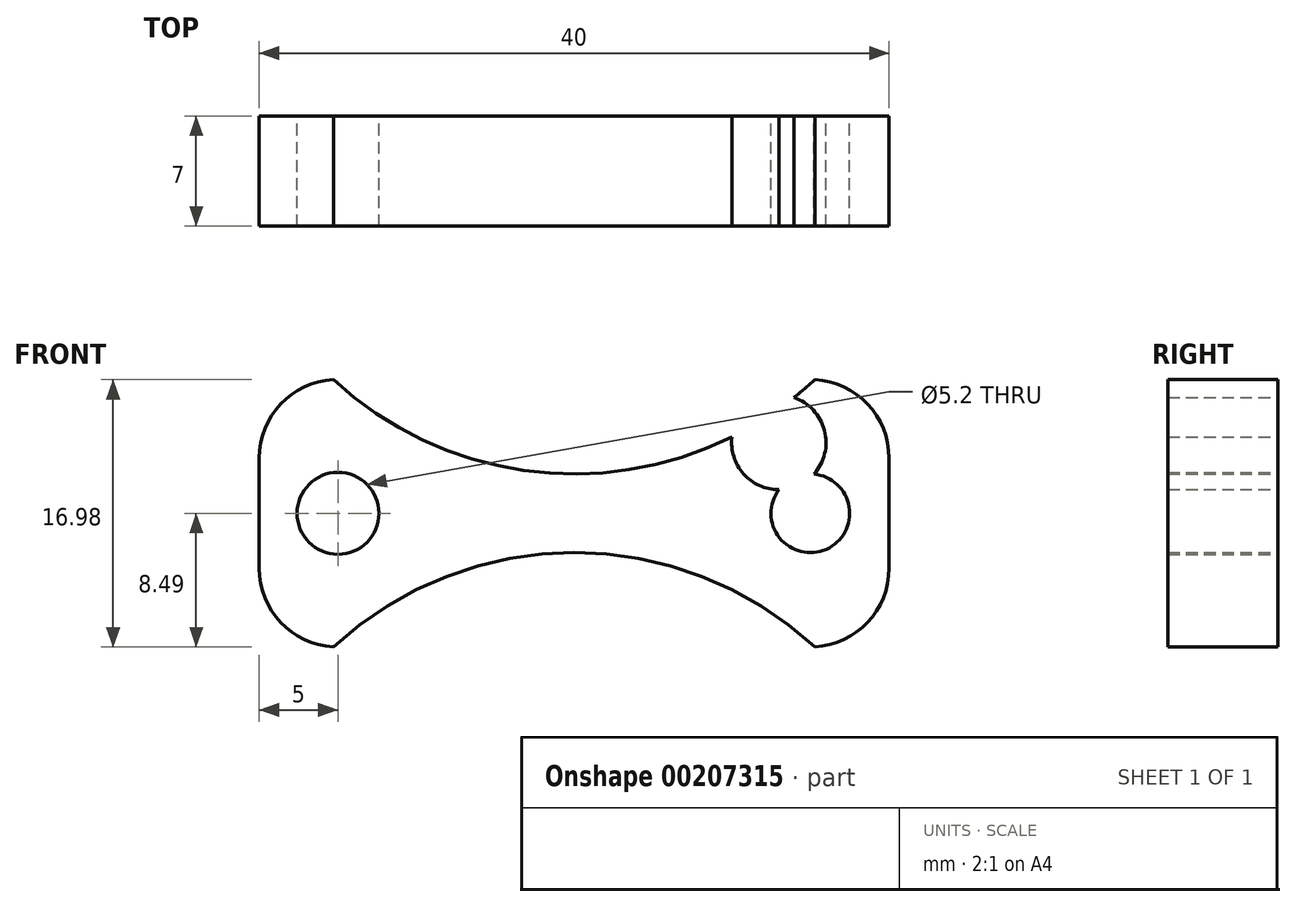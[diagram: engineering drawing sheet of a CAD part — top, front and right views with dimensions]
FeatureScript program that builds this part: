
annotation { "Feature Type Name" : "Feature", "Feature Type Description" : "" }
export const myFeature = defineFeature(function(context is Context, id is Id, definition is map)
    precondition{}
    {
        {
            var Q0;
            Q0=qCreatedBy(makeId("Front.planeOp"),FACE);
            var sketch = newSketch(context, id + "F0", { "sketchPlane" : qUnion([Q0])});
            skLineSegment(sketch, "E0.bottom", {"start": v(15, -8.5) * mm, "end": v(-15, -8.5) * mm});
            skLineSegment(sketch, "E0.top", {"start": v(15, 8.5) * mm, "end": v(-15, 8.5) * mm});
            skLineSegment(sketch, "E0.left", {"start": v(20, -3.5) * mm, "end": v(20, 3.5) * mm});
            skLineSegment(sketch, "E0.right", {"start": v(-20, -3.5) * mm, "end": v(-20, 3.5) * mm});
            skPoint(sketch, "E0.middle", {"position": v(0, 0) * mm});
            skPoint(sketch, "E1.visualSharp", {"position": v(-20, 8.5) * mm});
            skArc(sketch, "E1.filletArc", {"start": v(-15, 8.5) * mm, "mid": v(-18.54, 7.04) * mm, "end": v(-20, 3.5) * mm});
            skPoint(sketch, "E2.visualSharp", {"position": v(-20, -8.5) * mm});
            skArc(sketch, "E2.filletArc", {"start": v(-20, -3.5) * mm, "mid": v(-18.54, -7.04) * mm, "end": v(-15, -8.5) * mm});
            skPoint(sketch, "E3.visualSharp", {"position": v(20, -8.5) * mm});
            skArc(sketch, "E3.filletArc", {"start": v(15, -8.5) * mm, "mid": v(18.54, -7.04) * mm, "end": v(20, -3.5) * mm});
            skPoint(sketch, "E4.visualSharp", {"position": v(20, 8.5) * mm});
            skArc(sketch, "E4.filletArc", {"start": v(20, 3.5) * mm, "mid": v(18.54, 7.04) * mm, "end": v(15, 8.5) * mm});
            skLineSegment(sketch, "E5", {"start": v(0, 0) * mm, "end": v(15, 0) * mm});
            skSolve(sketch);
        }
        {
            var Q0;
            Q0=makeQuery(id+"F0.imprint","IMPRINT",FACE,{"disambiguationData":[TD([[makeQuery(id+"F0.imprint","IMPRINT",EDGE,{"derivedFrom":sQuery(id+"F0.wireOp",EDGE,"E0.bottom")}),-1.0]])]});
            extrude(context, id + "F1", {"entities" : qUnion([Q0]), "depth" : 7 * mm});
        }
        {
            var Q0;
            Q0=qCreatedBy(makeId("Front.planeOp"),FACE);
            var sketch = newSketch(context, id + "F2", { "sketchPlane" : qUnion([Q0])});
            skLineSegment(sketch, "E6", {"start": v(0, 0) * mm, "end": v(-15, 0) * mm});
            skPoint(sketch, "E7", {"position": v(-15, 0) * mm});
            skSolve(sketch);
        }
        {
            var Q0;
            Q0=sQuery(id+"F2.wireOp",VERTEX,"E7");
            var Q1;
            Q1=makeQuery(id+"F1.opExtrude","SWEPT_BODY",BODY,{"disambiguationData":[OSD([sQuery(id+"F0.wireOp",EDGE,"E0.bottom"),sQuery(id+"F0.wireOp",EDGE,"E0.top"),sQuery(id+"F0.wireOp",EDGE,"E0.left"),sQuery(id+"F0.wireOp",EDGE,"E0.right"),sQuery(id+"F0.wireOp",EDGE,"E1.filletArc"),sQuery(id+"F0.wireOp",EDGE,"E2.filletArc"),sQuery(id+"F0.wireOp",EDGE,"E3.filletArc"),sQuery(id+"F0.wireOp",EDGE,"E4.filletArc")])]});
            hole(context, id + "F3", {"style" : HoleStyle.SIMPLE, "endStyle" : HoleEndStyle.THROUGH, "oppositeDirection" : true, "holeDiameter" : 5.2 * mm, "locations" : qUnion([Q0]), "scope" : qUnion([Q1]), "isTappedThrough" : true});
        }
        {
            var Q0;
            Q0=qCreatedBy(makeId("Front.planeOp"),FACE);
            var sketch = newSketch(context, id + "F4", { "sketchPlane" : qUnion([Q0])});
            skLineSegment(sketch, "E8", {"start": v(0, 0) * mm, "end": v(15, 0) * mm});
            skPoint(sketch, "E9", {"position": v(15, 0) * mm});
            skSolve(sketch);
        }
        {
            var Q0;
            Q0=sQuery(id+"F4.wireOp",VERTEX,"E9");
            var Q1;
            Q1=makeQuery(id+"F1.opExtrude","SWEPT_BODY",BODY,{"disambiguationData":[OSD([sQuery(id+"F0.wireOp",EDGE,"E0.bottom"),sQuery(id+"F0.wireOp",EDGE,"E0.top"),sQuery(id+"F0.wireOp",EDGE,"E0.left"),sQuery(id+"F0.wireOp",EDGE,"E0.right"),sQuery(id+"F0.wireOp",EDGE,"E1.filletArc"),sQuery(id+"F0.wireOp",EDGE,"E2.filletArc"),sQuery(id+"F0.wireOp",EDGE,"E3.filletArc"),sQuery(id+"F0.wireOp",EDGE,"E4.filletArc")])]});
            hole(context, id + "F5", {"style" : HoleStyle.SIMPLE, "endStyle" : HoleEndStyle.THROUGH, "oppositeDirection" : true, "holeDiameter" : 5 * mm, "locations" : qUnion([Q0]), "scope" : qUnion([Q1]), "isTappedThrough" : true});
        }
        {
            var Q0;
            Q0=qCreatedBy(makeId("Front.planeOp"),FACE);
            var sketch = newSketch(context, id + "F6", { "sketchPlane" : qUnion([Q0])});
            skLineSegment(sketch, "E10", {"start": v(0, 0) * mm, "end": v(0, -25) * mm});
            skPoint(sketch, "E11", {"position": v(0, -25) * mm});
            skSolve(sketch);
        }
        {
            var Q0;
            Q0=sQuery(id+"F6.wireOp",VERTEX,"E11");
            var Q1;
            Q1=makeQuery(id+"F1.opExtrude","SWEPT_BODY",BODY,{"disambiguationData":[OSD([sQuery(id+"F0.wireOp",EDGE,"E0.bottom"),sQuery(id+"F0.wireOp",EDGE,"E0.top"),sQuery(id+"F0.wireOp",EDGE,"E0.left"),sQuery(id+"F0.wireOp",EDGE,"E0.right"),sQuery(id+"F0.wireOp",EDGE,"E1.filletArc"),sQuery(id+"F0.wireOp",EDGE,"E2.filletArc"),sQuery(id+"F0.wireOp",EDGE,"E3.filletArc"),sQuery(id+"F0.wireOp",EDGE,"E4.filletArc")])]});
            hole(context, id + "F7", {"style" : HoleStyle.SIMPLE, "endStyle" : HoleEndStyle.THROUGH, "oppositeDirection" : true, "holeDiameter" : 45 * mm, "locations" : qUnion([Q0]), "scope" : qUnion([Q1]), "isTappedThrough" : true});
        }
        {
            var Q0;
            Q0=qCreatedBy(makeId("Front.planeOp"),FACE);
            var sketch = newSketch(context, id + "F8", { "sketchPlane" : qUnion([Q0])});
            skLineSegment(sketch, "E12", {"start": v(0, 0) * mm, "end": v(0, 25) * mm});
            skPoint(sketch, "E13", {"position": v(0, 25) * mm});
            skSolve(sketch);
        }
        {
            var Q0;
            Q0=sQuery(id+"F8.wireOp",VERTEX,"E13");
            var Q1;
            Q1=makeQuery(id+"F1.opExtrude","SWEPT_BODY",BODY,{"disambiguationData":[OSD([sQuery(id+"F0.wireOp",EDGE,"E0.bottom"),sQuery(id+"F0.wireOp",EDGE,"E0.top"),sQuery(id+"F0.wireOp",EDGE,"E0.left"),sQuery(id+"F0.wireOp",EDGE,"E0.right"),sQuery(id+"F0.wireOp",EDGE,"E1.filletArc"),sQuery(id+"F0.wireOp",EDGE,"E2.filletArc"),sQuery(id+"F0.wireOp",EDGE,"E3.filletArc"),sQuery(id+"F0.wireOp",EDGE,"E4.filletArc")])]});
            hole(context, id + "F9", {"style" : HoleStyle.SIMPLE, "endStyle" : HoleEndStyle.THROUGH, "oppositeDirection" : true, "holeDiameter" : 45 * mm, "locations" : qUnion([Q0]), "scope" : qUnion([Q1]), "isTappedThrough" : true});
        }
        {
            var Q0;
            Q0=qCreatedBy(makeId("Front.planeOp"),FACE);
            var sketch = newSketch(context, id + "F10", { "sketchPlane" : qUnion([Q0])});
            skLineSegment(sketch, "E14", {"start": v(0, 0) * mm, "end": v(13, 0) * mm});
            skLineSegment(sketch, "E15", {"start": v(13, 0) * mm, "end": v(13, 4.5) * mm});
            skPoint(sketch, "E16", {"position": v(13, 4.5) * mm});
            skSolve(sketch);
        }
        {
            var Q0;
            Q0=sQuery(id+"F10.wireOp",VERTEX,"E16");
            var Q1;
            Q1=makeQuery(id+"F1.opExtrude","SWEPT_BODY",BODY,{"disambiguationData":[OSD([sQuery(id+"F0.wireOp",EDGE,"E0.bottom"),sQuery(id+"F0.wireOp",EDGE,"E0.top"),sQuery(id+"F0.wireOp",EDGE,"E0.left"),sQuery(id+"F0.wireOp",EDGE,"E0.right"),sQuery(id+"F0.wireOp",EDGE,"E1.filletArc"),sQuery(id+"F0.wireOp",EDGE,"E2.filletArc"),sQuery(id+"F0.wireOp",EDGE,"E3.filletArc"),sQuery(id+"F0.wireOp",EDGE,"E4.filletArc")])]});
            hole(context, id + "F11", {"style" : HoleStyle.SIMPLE, "endStyle" : HoleEndStyle.THROUGH, "oppositeDirection" : true, "holeDiameter" : 6 * mm, "locations" : qUnion([Q0]), "scope" : qUnion([Q1]), "isTappedThrough" : true});
        }
    });
